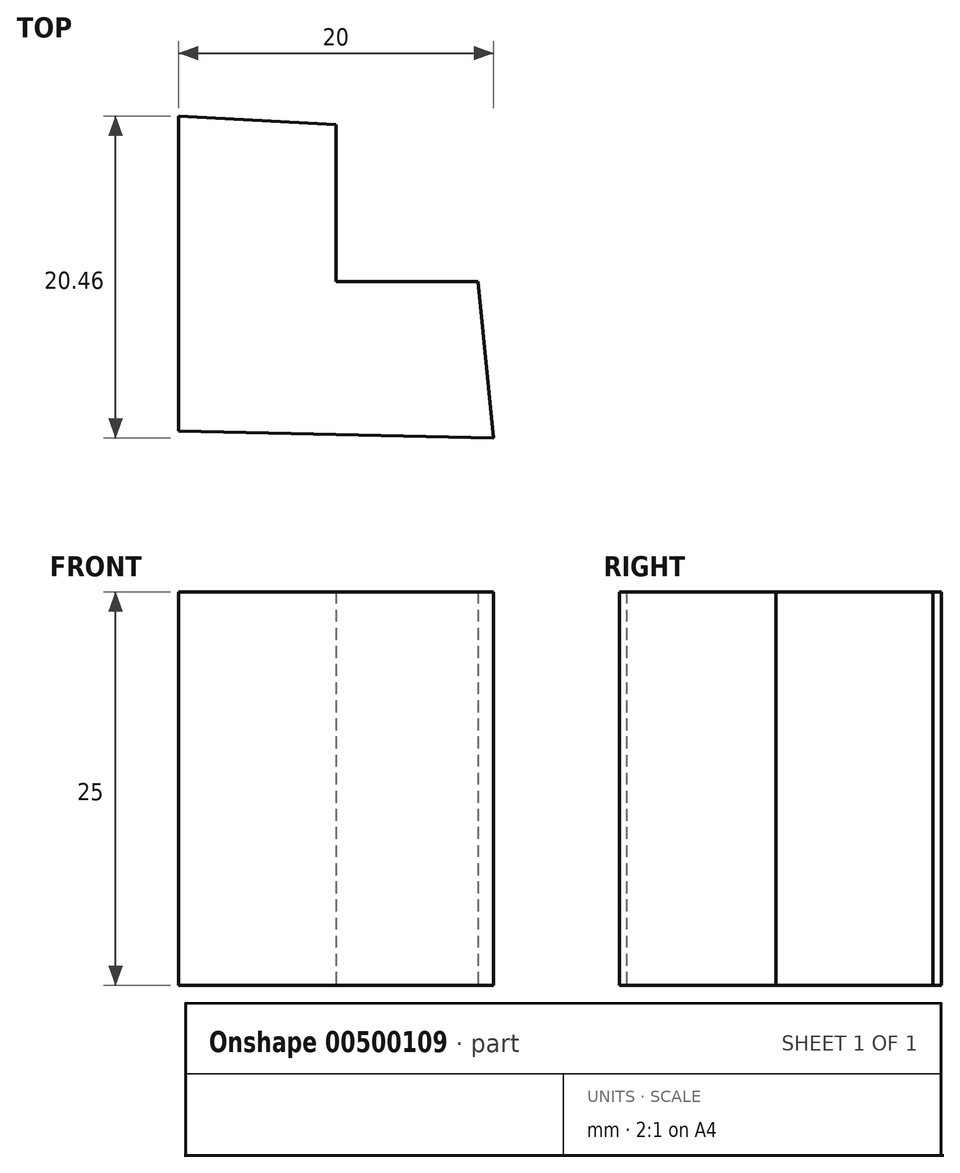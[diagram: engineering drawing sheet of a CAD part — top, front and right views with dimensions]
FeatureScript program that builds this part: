
annotation { "Feature Type Name" : "Feature", "Feature Type Description" : "" }
export const myFeature = defineFeature(function(context is Context, id is Id, definition is map)
    precondition{}
    {
        {
            var Q0;
            Q0=qCreatedBy(makeId("Top.planeOp"),FACE);
            var sketch = newSketch(context, id + "F0", { "sketchPlane" : qUnion([Q0])});
            skLineSegment(sketch, "E0", {"start": v(-42, -18.37) * mm, "end": v(-42, -38.37) * mm});
            skLineSegment(sketch, "E1", {"start": v(-22, -38.83) * mm, "end": v(-42, -38.37) * mm});
            skLineSegment(sketch, "E2", {"start": v(-23, -28.88) * mm, "end": v(-32.01, -28.88) * mm});
            skLineSegment(sketch, "E3", {"start": v(-32.01, -28.88) * mm, "end": v(-32.01, -18.92) * mm});
            skLineSegment(sketch, "E4", {"start": v(-32.01, -18.92) * mm, "end": v(-42, -18.37) * mm});
            skLineSegment(sketch, "E5", {"start": v(-23, -28.88) * mm, "end": v(-22, -38.83) * mm});
            skLineSegment(sketch, "E6", {"start": v(13.46, -14.52) * mm, "end": v(13.46, -34.52) * mm});
            skLineSegment(sketch, "E7", {"start": v(33.46, -34.52) * mm, "end": v(33.46, -24.52) * mm});
            skLineSegment(sketch, "E8", {"start": v(33.46, -24.52) * mm, "end": v(23.46, -24.52) * mm});
            skLineSegment(sketch, "E9", {"start": v(33.46, -34.52) * mm, "end": v(13.46, -34.52) * mm});
            skLineSegment(sketch, "E10", {"start": v(23.46, -24.52) * mm, "end": v(23.46, -14.52) * mm});
            skLineSegment(sketch, "E11", {"start": v(23.46, -14.52) * mm, "end": v(13.46, -14.52) * mm});
            skSolve(sketch);
        }
        {
            var Q0;
            Q0 = qSketchRegion(id + "F0", true);
            extrude(context, id + "F1", {"entities" : qUnion([Q0]), "depth" : 25 * mm});
        }
        {
            var Q0;
            Q0=makeQuery(id+"F1.opExtrude","SWEPT_BODY",BODY,{"disambiguationData":[OSD([sQuery(id+"F0.wireOp",EDGE,"E6"),sQuery(id+"F0.wireOp",EDGE,"E7"),sQuery(id+"F0.wireOp",EDGE,"E8"),sQuery(id+"F0.wireOp",EDGE,"E9"),sQuery(id+"F0.wireOp",EDGE,"E10"),sQuery(id+"F0.wireOp",EDGE,"E11")])]});
            deleteBodies(context, id + "F2", {"entities" : qUnion([Q0])});
        }
    });
